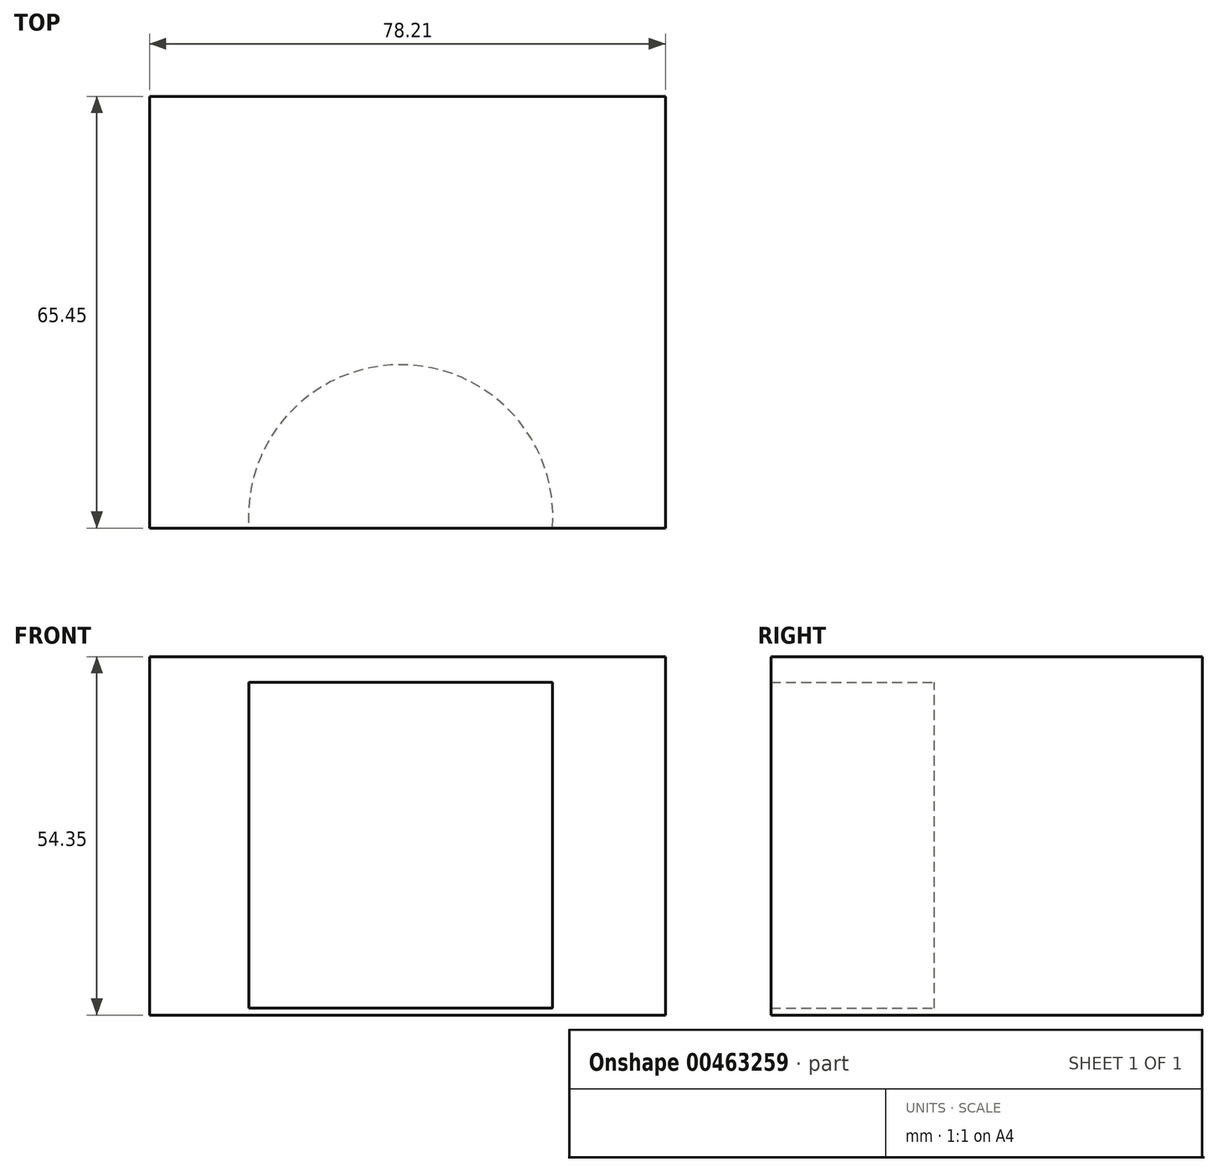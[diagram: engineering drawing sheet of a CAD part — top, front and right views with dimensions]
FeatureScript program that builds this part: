
annotation { "Feature Type Name" : "Feature", "Feature Type Description" : "" }
export const myFeature = defineFeature(function(context is Context, id is Id, definition is map)
    precondition{}
    {
        {
            var Q0;
            Q0=qCreatedBy(makeId("Front.planeOp"),FACE);
            var sketch = newSketch(context, id + "F0", { "sketchPlane" : qUnion([Q0])});
            skLineSegment(sketch, "E0.bottom", {"start": v(-38.06, -50.47) * mm, "end": v(40.15, -50.47) * mm});
            skLineSegment(sketch, "E0.top", {"start": v(-38.06, 3.88) * mm, "end": v(40.15, 3.88) * mm});
            skLineSegment(sketch, "E0.left", {"start": v(-38.06, 3.88) * mm, "end": v(-38.06, -50.47) * mm});
            skLineSegment(sketch, "E0.right", {"start": v(40.15, 3.88) * mm, "end": v(40.15, -50.47) * mm});
            skSolve(sketch);
        }
        {
            var Q0;
            Q0 = qSketchRegion(id + "F0", true);
            extrude(context, id + "F1", {"entities" : qUnion([Q0]), "depth" : 65.45 * mm});
        }
        {
            var Q0;
            Q0=qCreatedBy(makeId("Top.planeOp"),FACE);
            var sketch = newSketch(context, id + "F2", { "sketchPlane" : qUnion([Q0])});
            skCircle(sketch, "E1", {"center": v(0, -36.95) * mm, "radius": 0.9 * mm});
            skCircle(sketch, "E2", {"center": v(0, -63.77) * mm, "radius": 23.1 * mm});
            skSolve(sketch);
        }
        {
            var Q0;
            Q0=makeQuery(id+"F2.imprint","IMPRINT",FACE,{"disambiguationData":[TD([[makeQuery(id+"F2.imprint","IMPRINT",EDGE,{"derivedFrom":sQuery(id+"F2.wireOp",EDGE,"E2")}),1.0]])]});
            extrude(context, id + "F3", {"entities" : qUnion([Q0]), "operationType" : NewBodyOperationType.REMOVE, "oppositeDirection" : true, "depth" : 49.43 * mm});
        }
    });
